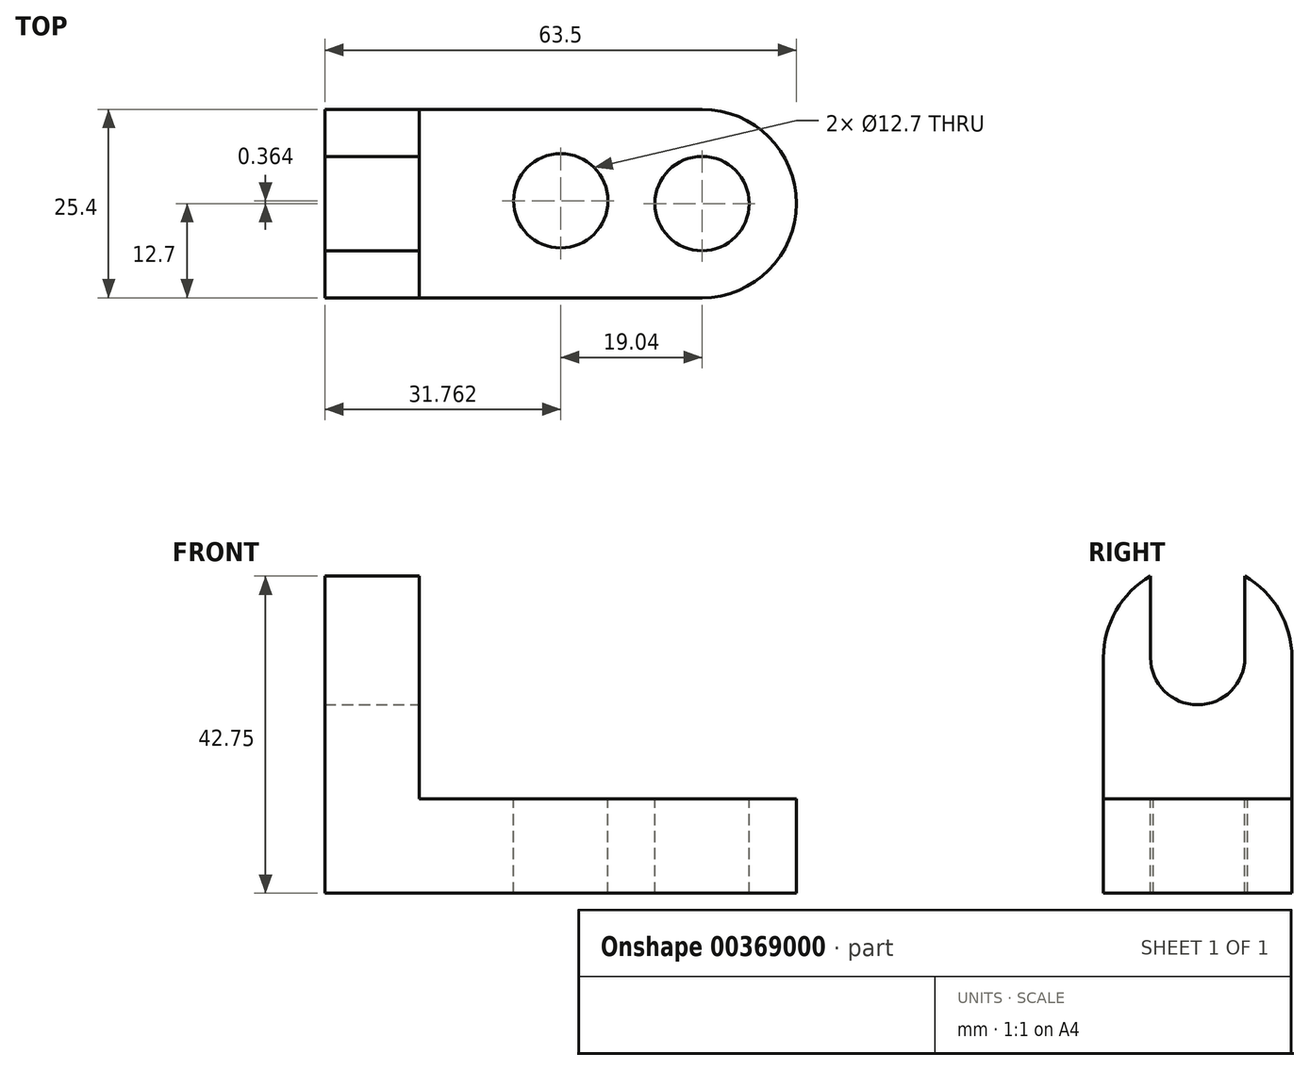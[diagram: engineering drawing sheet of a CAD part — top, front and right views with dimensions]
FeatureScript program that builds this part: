
annotation { "Feature Type Name" : "Feature", "Feature Type Description" : "" }
export const myFeature = defineFeature(function(context is Context, id is Id, definition is map)
    precondition{}
    {
        {
            var Q0;
            Q0=qCreatedBy(makeId("Front.planeOp"),FACE);
            var sketch = newSketch(context, id + "F0", { "sketchPlane" : qUnion([Q0])});
            skLineSegment(sketch, "E0", {"start": v(-42.1, 0) * mm, "end": v(21.4, 0) * mm});
            skLineSegment(sketch, "E1", {"start": v(21.4, 0) * mm, "end": v(21.4, 12.7) * mm});
            skLineSegment(sketch, "E2", {"start": v(21.4, 12.7) * mm, "end": v(-42.1, 12.7) * mm});
            skLineSegment(sketch, "E3", {"start": v(-42.1, 12.7) * mm, "end": v(-42.1, 0) * mm});
            skLineSegment(sketch, "E4", {"start": v(-42.1, 12.7) * mm, "end": v(-42.1, 44.45) * mm});
            skLineSegment(sketch, "E5", {"start": v(-42.1, 44.45) * mm, "end": v(-29.4, 44.45) * mm});
            skLineSegment(sketch, "E6", {"start": v(-29.4, 44.45) * mm, "end": v(-29.4, 12.7) * mm});
            skSolve(sketch);
        }
        {
            var Q0;
            Q0=makeQuery(id+"F0.imprint","IMPRINT",FACE,{"disambiguationData":[TD([[makeQuery(id+"F0.imprint","IMPRINT",EDGE,{"derivedFrom":sQuery(id+"F0.wireOp",EDGE,"E0")}),1.0]])]});
            var Q1;
            {var subQ0=sQuery(id+"F0.wireOp",EDGE,"E4");Q1=makeQuery(id+"F0.imprint","IMPRINT",FACE,{"disambiguationData":[TD([[makeQuery(id+"F0.imprint","IMPRINT",EDGE,{"derivedFrom":subQ0}),-1.0]])]});}
            extrude(context, id + "F1", {"entities" : qUnion([Q0, Q1]), "depth" : 25.4 * mm});
        }
        {
            var Q0;
            Q0=makeQuery(id+"F1.opExtrude","SWEPT_FACE",FACE,{"disambiguationData":[OSD([sQuery(id+"F0.wireOp",EDGE,"E2")])]});
            var sketch = newSketch(context, id + "F2", { "sketchPlane" : qUnion([Q0])});
            skLineSegment(sketch, "E7", {"start": v(-29.4, 0) * mm, "end": v(8.7, 0) * mm});
            skLineSegment(sketch, "E8", {"start": v(21.4, -12.7) * mm, "end": v(21.4, -25.4) * mm});
            skLineSegment(sketch, "E9", {"start": v(21.4, -25.4) * mm, "end": v(-29.4, -25.4) * mm});
            skLineSegment(sketch, "E10", {"start": v(-29.4, -25.4) * mm, "end": v(-29.4, 0) * mm});
            skPoint(sketch, "E11.visualSharp", {"position": v(21.4, 0) * mm});
            skArc(sketch, "E11.filletArc", {"start": v(21.4, -12.7) * mm, "mid": v(17.68, -3.72) * mm, "end": v(8.7, 0) * mm});
            skCircle(sketch, "E12", {"center": v(8.7, -12.7) * mm, "radius": 6.35 * mm});
            skLineSegment(sketch, "E13", {"start": v(15.05, -12.7) * mm, "end": v(21.4, -12.7) * mm});
            skLineSegment(sketch, "E14", {"start": v(8.7, -12.7) * mm, "end": v(8.7, -6.35) * mm});
            skLineSegment(sketch, "E15", {"start": v(2.36, -12.34) * mm, "end": v(-3.99, -12.34) * mm});
            skLineSegment(sketch, "E16", {"start": v(-3.99, -12.34) * mm, "end": v(-10.34, -12.34) * mm});
            skCircle(sketch, "E17", {"center": v(-10.34, -12.34) * mm, "radius": 6.35 * mm});
            skSolve(sketch);
        }
        {
            var Q0;
            Q0=makeQuery(id+"F2.imprint","IMPRINT",FACE,{"disambiguationData":[TD([[makeQuery(id+"F2.imprint","IMPRINT",EDGE,{"derivedFrom":sQuery(id+"F2.wireOp",EDGE,"E17")}),1.0]])]});
            var Q1;
            {var subQ0=sQuery(id+"F2.wireOp",EDGE,"E12");var subQ1=makeQuery(id+"F2.imprint","IMPRINT",VERTEX,{"disambiguationData":[OD(0.0)],"derivedFrom":subQ0});Q1=makeQuery(id+"F2.imprint","IMPRINT",FACE,{"disambiguationData":[TD([[makeQuery(id+"F2.imprint","IMPRINT",EDGE,{"disambiguationData":[TD([[subQ1,-1.0]])],"derivedFrom":subQ0}),1.0]])]});}
            var Q2;
            {var subQ0=sQuery(id+"F2.wireOp",EDGE,"E11.filletArc");Q2=makeQuery(id+"F2.imprint","IMPRINT",FACE,{"disambiguationData":[TD([[makeQuery(id+"F2.imprint","IMPRINT",EDGE,{"derivedFrom":subQ0}),-1.0]])]});}
            extrude(context, id + "F3", {"entities" : qUnion([Q0, Q1, Q2]), "operationType" : NewBodyOperationType.REMOVE, "oppositeDirection" : true, "depth" : 25.4 * mm});
        }
        {
            var Q0;
            Q0=makeQuery(id+"F1.opExtrude","SWEPT_FACE",FACE,{"disambiguationData":[OSD([sQuery(id+"F0.wireOp",EDGE,"E2")])]});
            var sketch = newSketch(context, id + "F4", { "sketchPlane" : qUnion([Q0])});
            skLineSegment(sketch, "E18", {"start": v(-29.4, 0) * mm, "end": v(-29.4, -25.4) * mm});
            skLineSegment(sketch, "E19", {"start": v(-29.4, -25.4) * mm, "end": v(8.7, -25.4) * mm});
            skLineSegment(sketch, "E20", {"start": v(21.4, -12.7) * mm, "end": v(21.4, 0) * mm});
            skLineSegment(sketch, "E21", {"start": v(21.4, 0) * mm, "end": v(-29.4, 0) * mm});
            skPoint(sketch, "E22.visualSharp", {"position": v(21.4, -25.4) * mm});
            skArc(sketch, "E22.filletArc", {"start": v(8.7, -25.4) * mm, "mid": v(17.68, -21.68) * mm, "end": v(21.4, -12.7) * mm});
            skSolve(sketch);
        }
        {
            var Q0;
            {var subQ0=sQuery(id+"F4.wireOp",EDGE,"E20");Q0=makeQuery(id+"F4.imprint","IMPRINT",FACE,{"disambiguationData":[TD([[makeQuery(id+"F4.imprint","IMPRINT",EDGE,{"derivedFrom":subQ0}),1.0]])]});}
            var Q1;
            Q1=makeQuery(id+"F4.imprint","IMPRINT",FACE,{"disambiguationData":[TD([[makeQuery(id+"F4.imprint","IMPRINT",EDGE,{"derivedFrom":makeQuery(id+"F3.boolean.opBoolean","COPY",EDGE,{"derivedFrom":makeQuery(id+"F3.opExtrude","CAP_EDGE",EDGE,{"disambiguationData":[OSD([sQuery(id+"F2.wireOp",EDGE,"E12")])],"isStart":true})})}),1.0]])]});
            var Q2;
            Q2=makeQuery(id+"F4.imprint","IMPRINT",FACE,{"disambiguationData":[TD([[makeQuery(id+"F4.imprint","IMPRINT",EDGE,{"derivedFrom":makeQuery(id+"F3.boolean.opBoolean","COPY",EDGE,{"derivedFrom":makeQuery(id+"F3.opExtrude","CAP_EDGE",EDGE,{"disambiguationData":[OSD([sQuery(id+"F2.wireOp",EDGE,"E17")])],"isStart":true})})}),1.0]])]});
            var Q3;
            {var subQ0=sQuery(id+"F4.wireOp",EDGE,"E22.filletArc");Q3=makeQuery(id+"F4.imprint","IMPRINT",FACE,{"disambiguationData":[TD([[makeQuery(id+"F4.imprint","IMPRINT",EDGE,{"derivedFrom":subQ0}),-1.0]])]});}
            extrude(context, id + "F5", {"entities" : qUnion([Q0, Q1, Q2, Q3]), "operationType" : NewBodyOperationType.REMOVE, "oppositeDirection" : true, "depth" : 25.4 * mm});
        }
        {
            var Q0;
            Q0=makeQuery(id+"F1.opExtrude","SWEPT_FACE",FACE,{"disambiguationData":[OSD([sQuery(id+"F0.wireOp",EDGE,"E6")])]});
            var sketch = newSketch(context, id + "F6", { "sketchPlane" : qUnion([Q0])});
            skLineSegment(sketch, "E23", {"start": v(-25.4, 31.75) * mm, "end": v(-25.4, 12.7) * mm});
            skLineSegment(sketch, "E24", {"start": v(-25.4, 12.7) * mm, "end": v(0, 12.7) * mm});
            skLineSegment(sketch, "E25", {"start": v(0, 12.7) * mm, "end": v(0, 44.45) * mm});
            skLineSegment(sketch, "E26", {"start": v(0, 44.45) * mm, "end": v(-12.7, 44.45) * mm});
            skPoint(sketch, "E27.visualSharp", {"position": v(-25.4, 44.45) * mm});
            skArc(sketch, "E27.filletArc", {"start": v(-12.7, 44.45) * mm, "mid": v(-21.68, 40.73) * mm, "end": v(-25.4, 31.75) * mm});
            skCircle(sketch, "E28", {"center": v(-12.7, 31.75) * mm, "radius": 6.35 * mm});
            skLineSegment(sketch, "E29", {"start": v(-12.7, 12.7) * mm, "end": v(-12.7, 25.4) * mm});
            skLineSegment(sketch, "E30", {"start": v(-19.05, 31.75) * mm, "end": v(-19.05, 44.45) * mm});
            skLineSegment(sketch, "E31", {"start": v(-6.35, 44.45) * mm, "end": v(-6.35, 31.75) * mm});
            skSolve(sketch);
        }
        {
            var Q0;
            {var subQ0=sQuery(id+"F6.wireOp",EDGE,"E28");var subQ1=makeQuery(id+"F6.imprint","INTERSECT",VERTEX,{"derivedFrom":[subQ0,sQuery(id+"F6.wireOp",EDGE,"E30")]});Q0=makeQuery(id+"F6.imprint","IMPRINT",FACE,{"disambiguationData":[TD([[makeQuery(id+"F6.imprint","IMPRINT",EDGE,{"disambiguationData":[TD([[subQ1,1.0]])],"derivedFrom":subQ0}),1.0]])]});}
            var Q1;
            {var subQ0=sQuery(id+"F6.wireOp",EDGE,"E27.filletArc");var subQ4=sQuery(id+"F6.wireOp",EDGE,"E30");var subQ5=makeQuery(id+"F6.imprint","INTERSECT",VERTEX,{"derivedFrom":[subQ0,subQ4]});Q1=makeQuery(id+"F6.imprint","IMPRINT",FACE,{"disambiguationData":[TD([[makeQuery(id+"F6.imprint","IMPRINT",EDGE,{"disambiguationData":[TD([[subQ5,-1.0]])],"derivedFrom":subQ0}),-1.0]])]});}
            var Q2;
            {var subQ0=sQuery(id+"F6.wireOp",EDGE,"E27.filletArc");var subQ3=sQuery(id+"F6.wireOp",EDGE,"E30");var subQ4=makeQuery(id+"F6.imprint","INTERSECT",VERTEX,{"derivedFrom":[subQ0,subQ3]});Q2=makeQuery(id+"F6.imprint","IMPRINT",FACE,{"disambiguationData":[TD([[makeQuery(id+"F6.imprint","IMPRINT",EDGE,{"disambiguationData":[TD([[subQ4,-1.0]])],"derivedFrom":subQ3}),-1.0]])]});}
            var Q3;
            {var subQ5=sQuery(id+"F6.wireOp",EDGE,"E31");Q3=makeQuery(id+"F6.imprint","IMPRINT",FACE,{"disambiguationData":[TD([[makeQuery(id+"F6.imprint","IMPRINT",EDGE,{"derivedFrom":subQ5}),-1.0]])]});}
            extrude(context, id + "F7", {"entities" : qUnion([Q0, Q1, Q2, Q3]), "operationType" : NewBodyOperationType.REMOVE, "oppositeDirection" : true, "depth" : 25.4 * mm});
        }
        {
            var Q0;
            Q0=makeQuery(id+"F1.opExtrude","SWEPT_FACE",FACE,{"disambiguationData":[OSD([sQuery(id+"F0.wireOp",EDGE,"E6")])]});
            var sketch = newSketch(context, id + "F8", { "sketchPlane" : qUnion([Q0])});
            skLineSegment(sketch, "E32", {"start": v(-25.4, 12.7) * mm, "end": v(0, 12.7) * mm});
            skLineSegment(sketch, "E33", {"start": v(0, 12.7) * mm, "end": v(0, 31.75) * mm});
            skLineSegment(sketch, "E34", {"start": v(-12.7, 44.45) * mm, "end": v(-25.4, 44.45) * mm});
            skLineSegment(sketch, "E35", {"start": v(-25.4, 44.45) * mm, "end": v(-25.4, 12.7) * mm});
            skPoint(sketch, "E36.visualSharp", {"position": v(0, 44.45) * mm});
            skArc(sketch, "E36.filletArc", {"start": v(0, 31.75) * mm, "mid": v(-3.72, 40.73) * mm, "end": v(-12.7, 44.45) * mm});
            skSolve(sketch);
        }
        {
            var Q0;
            {var subQ1=sQuery(id+"F8.wireOp",EDGE,"E34");Q0=makeQuery(id+"F8.imprint","IMPRINT",FACE,{"disambiguationData":[TD([[makeQuery(id+"F8.imprint","IMPRINT",EDGE,{"derivedFrom":subQ1}),1.0]])]});}
            var Q1;
            {var subQ1=sQuery(id+"F0.wireOp",EDGE,"E6");var subQ6=makeQuery(id+"F1.opExtrude","SWEPT_EDGE",EDGE,{"disambiguationData":[OSD([sQuery(id+"F0.wireOp",EDGE,"E5"),subQ1])]});Q1=makeQuery(id+"F8.imprint","IMPRINT",FACE,{"disambiguationData":[TD([[makeQuery(id+"F8.imprint","IMPRINT",EDGE,{"derivedFrom":subQ6}),-1.0]])]});}
            extrude(context, id + "F9", {"entities" : qUnion([Q0, Q1]), "operationType" : NewBodyOperationType.REMOVE, "oppositeDirection" : true, "depth" : 25.4 * mm});
        }
    });
